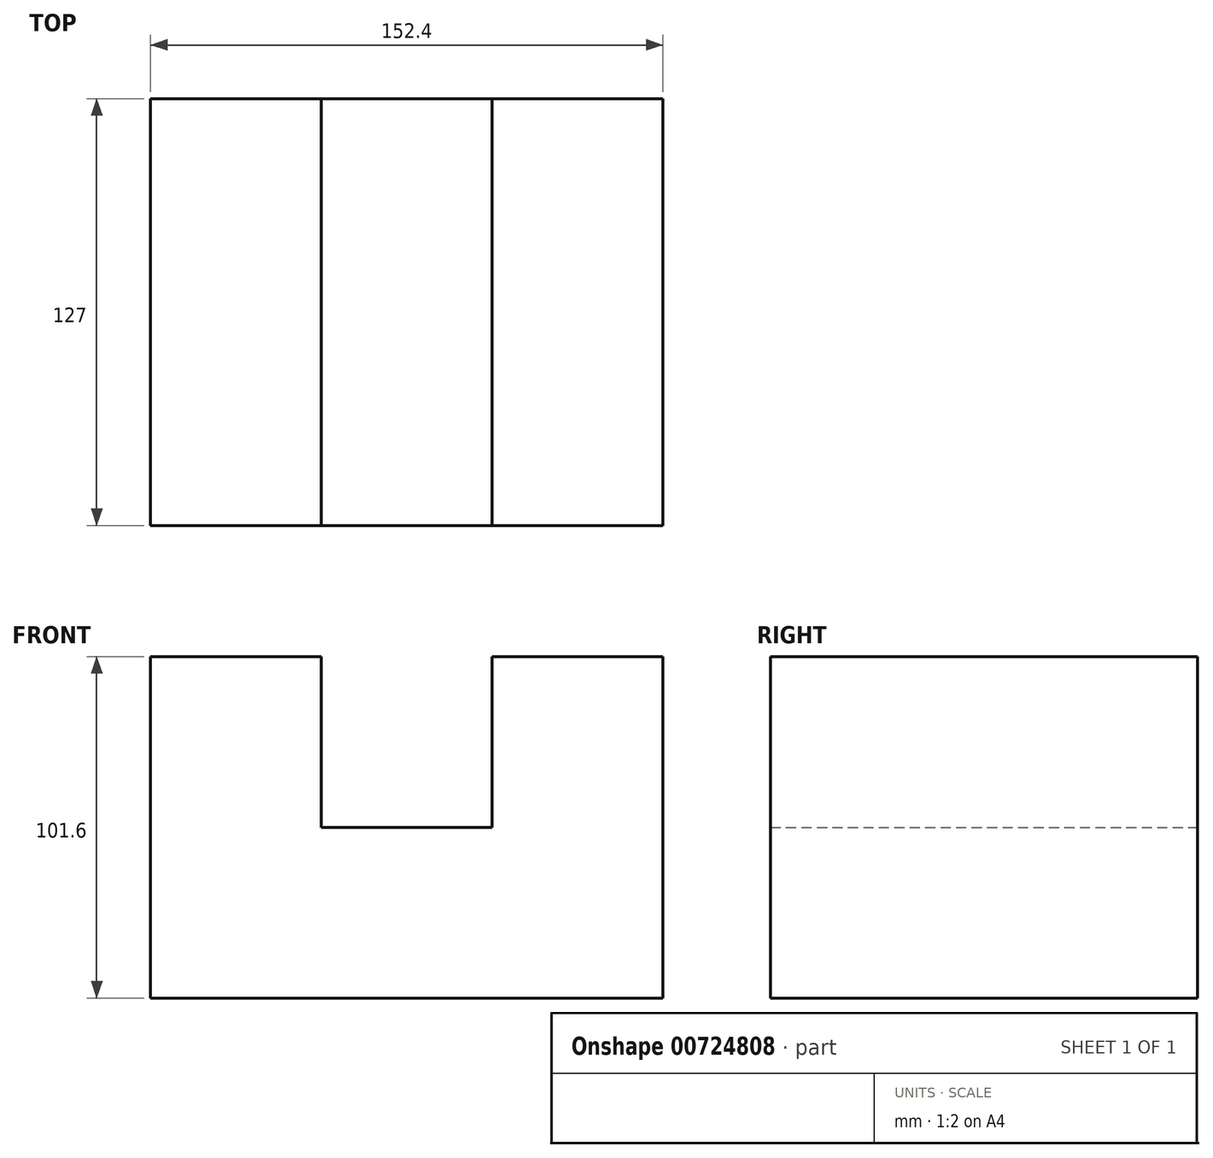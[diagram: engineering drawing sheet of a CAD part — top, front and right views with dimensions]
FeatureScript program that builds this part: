
annotation { "Feature Type Name" : "Feature", "Feature Type Description" : "" }
export const myFeature = defineFeature(function(context is Context, id is Id, definition is map)
    precondition{}
    {
        {
            var Q0;
            Q0=qCreatedBy(makeId("Front.planeOp"),FACE);
            var sketch = newSketch(context, id + "F0", { "sketchPlane" : qUnion([Q0])});
            skLineSegment(sketch, "E0", {"start": v(-50.8, -75.4) * mm, "end": v(101.6, -75.4) * mm});
            skLineSegment(sketch, "E1", {"start": v(101.6, -75.4) * mm, "end": v(101.6, 26.2) * mm});
            skLineSegment(sketch, "E2", {"start": v(101.6, 26.2) * mm, "end": v(50.8, 26.2) * mm});
            skLineSegment(sketch, "E3", {"start": v(50.8, 26.2) * mm, "end": v(50.8, -24.6) * mm});
            skLineSegment(sketch, "E4", {"start": v(50.8, -24.6) * mm, "end": v(0, -24.6) * mm});
            skLineSegment(sketch, "E5", {"start": v(0, -24.6) * mm, "end": v(0, 26.2) * mm});
            skLineSegment(sketch, "E6", {"start": v(0, 26.2) * mm, "end": v(-50.8, 26.2) * mm});
            skLineSegment(sketch, "E7", {"start": v(-50.8, 26.2) * mm, "end": v(-50.8, -75.4) * mm});
            skSolve(sketch);
        }
        {
            var Q0;
            Q0 = qSketchRegion(id + "F0", true);
            extrude(context, id + "F1", {"entities" : qUnion([Q0]), "depth" : 127 * mm, "offsetDistance" : 25.4 * mm});
        }
    });
